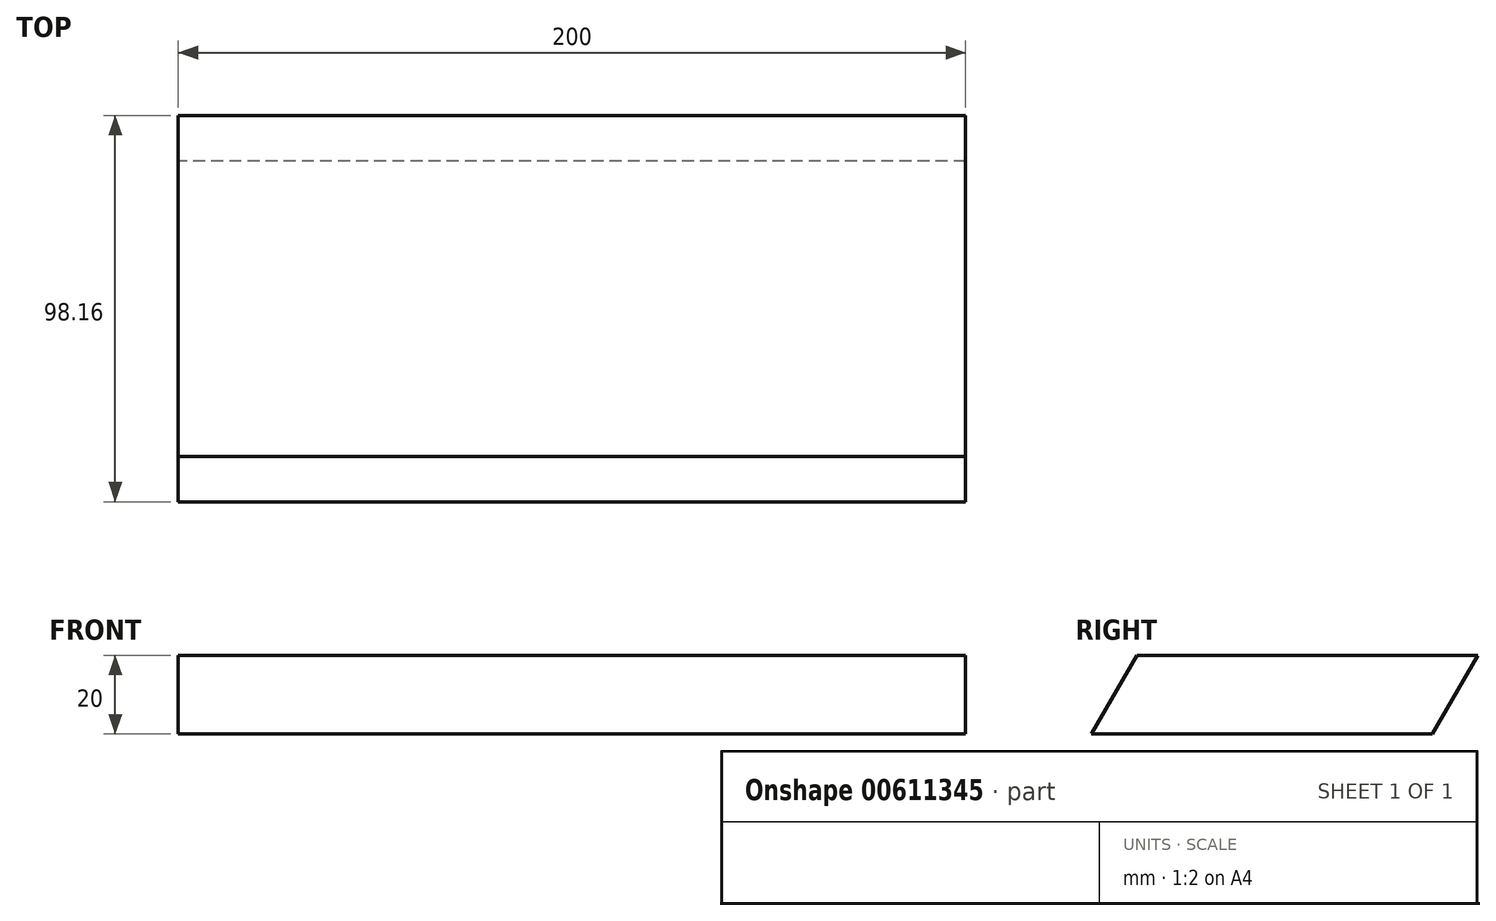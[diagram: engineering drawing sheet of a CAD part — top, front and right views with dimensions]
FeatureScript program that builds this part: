
annotation { "Feature Type Name" : "Feature", "Feature Type Description" : "" }
export const myFeature = defineFeature(function(context is Context, id is Id, definition is map)
    precondition{}
    {
        {
            var Q0;
            Q0=qCreatedBy(makeId("Top.planeOp"),FACE);
            var sketch = newSketch(context, id + "F0", { "sketchPlane" : qUnion([Q0])});
            skLineSegment(sketch, "E0.bottom", {"start": v(100, -49.07) * mm, "end": v(-100, -49.08) * mm});
            skLineSegment(sketch, "E0.top", {"start": v(100, 49.08) * mm, "end": v(-100, 49.08) * mm});
            skLineSegment(sketch, "E0.left", {"start": v(100, -49.07) * mm, "end": v(100, 49.08) * mm});
            skLineSegment(sketch, "E0.right", {"start": v(-100, -49.08) * mm, "end": v(-100, 49.08) * mm});
            skPoint(sketch, "E0.middle", {"position": v(0, 0) * mm});
            skSolve(sketch);
        }
        {
            var Q0;
            Q0=makeQuery(id+"F0.imprint","IMPRINT",FACE,{"disambiguationData":[TD([[makeQuery(id+"F0.imprint","IMPRINT",EDGE,{"derivedFrom":sQuery(id+"F0.wireOp",EDGE,"E0.bottom")}),-1.0]])]});
            extrude(context, id + "F1", {"entities" : qUnion([Q0]), "depth" : 20 * mm, "offsetDistance" : 25 * mm});
        }
        {
            var Q0;
            Q0=makeQuery(id+"F1.opExtrude","SWEPT_FACE",FACE,{"disambiguationData":[OSD([sQuery(id+"F0.wireOp",EDGE,"E0.right")])]});
            var sketch = newSketch(context, id + "F2", { "sketchPlane" : qUnion([Q0])});
            skLineSegment(sketch, "E1", {"start": v(-49.07, 20) * mm, "end": v(-37.53, 0) * mm});
            skLineSegment(sketch, "E2", {"start": v(-37.53, 0) * mm, "end": v(-37.53, 0) * mm});
            skLineSegment(sketch, "E3", {"start": v(-49.07, 0) * mm, "end": v(-49.07, 0) * mm});
            skLineSegment(sketch, "E4", {"start": v(-49.07, 0) * mm, "end": v(-37.53, 0) * mm});
            skLineSegment(sketch, "E5", {"start": v(-49.07, 0) * mm, "end": v(-49.07, 20) * mm});
            skLineSegment(sketch, "E6", {"start": v(49.08, 0) * mm, "end": v(37.53, 20) * mm});
            skLineSegment(sketch, "E7", {"start": v(37.53, 20) * mm, "end": v(37.53, 20) * mm});
            skLineSegment(sketch, "E8", {"start": v(49.08, 20) * mm, "end": v(37.53, 20) * mm});
            skLineSegment(sketch, "E9", {"start": v(49.08, 20) * mm, "end": v(49.08, 0) * mm});
            skSolve(sketch);
        }
        {
            var Q0;
            Q0 = qSketchRegion(id + "F2", true);
            extrude(context, id + "F3", {"entities" : qUnion([Q0]), "operationType" : NewBodyOperationType.REMOVE, "endBound" : BoundingType.THROUGH_ALL, "oppositeDirection" : true, "depth" : 25 * mm, "offsetDistance" : 25 * mm});
        }
        {
            var Q0;
            Q0 = qSketchRegion(id + "F2", true);
            extrude(context, id + "F4", {"entities" : qUnion([Q0]), "operationType" : NewBodyOperationType.REMOVE, "endBound" : BoundingType.THROUGH_ALL, "oppositeDirection" : true, "depth" : 25 * mm, "offsetDistance" : 25 * mm});
        }
    });
